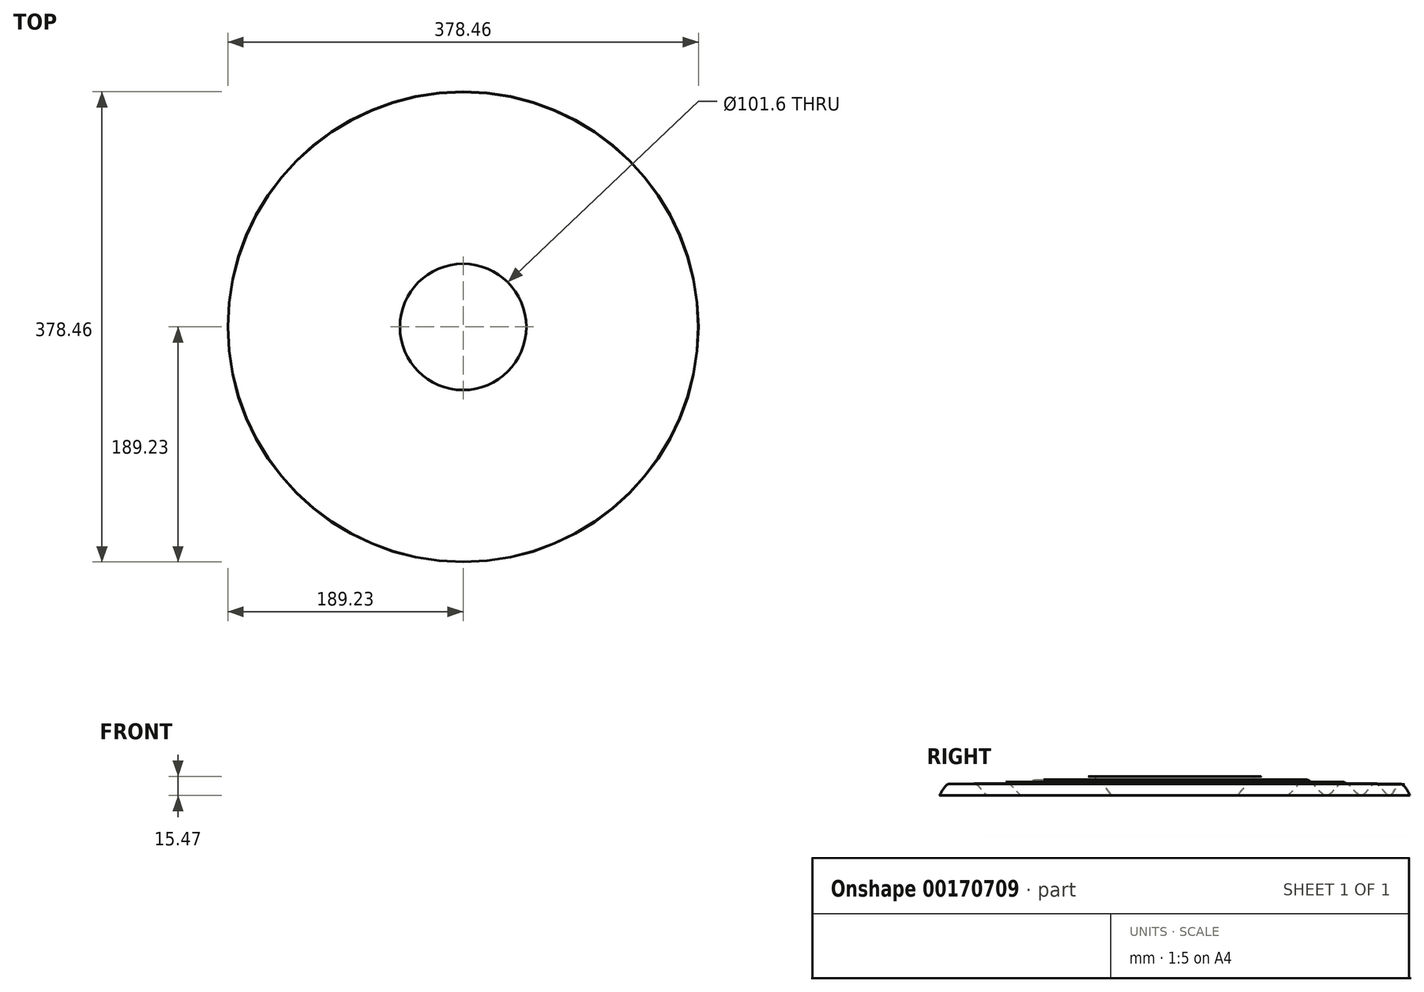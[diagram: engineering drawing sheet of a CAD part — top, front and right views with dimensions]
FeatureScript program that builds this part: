
annotation { "Feature Type Name" : "Feature", "Feature Type Description" : "" }
export const myFeature = defineFeature(function(context is Context, id is Id, definition is map)
    precondition{}
    {
        {
            var Q0;
            Q0=qCreatedBy(makeId("Front.planeOp"),FACE);
            var sketch = newSketch(context, id + "F0", { "sketchPlane" : qUnion([Q0])});
            skLineSegment(sketch, "E0", {"start": v(0, 51.98) * mm, "end": v(0, -57.5) * mm, "construction": true});
            skLineSegment(sketch, "E1", {"start": v(0, 38.1) * mm, "end": v(168.3, 13.53) * mm, "construction": true});
            skFitSpline(sketch, "E2", {"points": [v(50.8, 13.97) * mm, v(69.85, 27.9) * mm, v(88.9, 11.43) * mm, v(105.41, 22.71) * mm, v(121.92, 8.9) * mm, v(135.9, 18.26) * mm, v(149.86, 6.35) * mm, v(161.3, 14.55) * mm, v(172.72, 3.81) * mm, v(181.6, 11.59) * mm, v(189.23, 1.27) * mm], "startDerivative": vector(17.08, 50.9) * mm, "endDerivative": vector(25, -25.35) * mm, "construction": true});
            skFitSpline(sketch, "E3", {"points": [v(50.8, 0) * mm, v(69.85, 15.2) * mm, v(88.9, 0) * mm, v(105.41, 12.55) * mm, v(121.92, 0) * mm, v(135.9, 10.64) * mm, v(149.86, 0) * mm, v(161.3, 9.47) * mm, v(172.72, 0) * mm, v(181.61, 9.05) * mm, v(189.23, 0) * mm], "startDerivative": vector(16.8, 29.97) * mm, "endDerivative": vector(26.01, -29.79) * mm});
            skFitSpline(sketch, "E4", {"points": [v(50.8, 13.72) * mm, v(69.85, 27.65) * mm, v(88.9, 11.18) * mm, v(105.41, 22.46) * mm, v(121.92, 8.64) * mm, v(135.9, 18) * mm, v(149.86, 6.1) * mm, v(161.3, 14.3) * mm, v(172.72, 3.56) * mm, v(181.61, 11.33) * mm, v(189.23, 1.02) * mm], "startDerivative": vector(17.08, 35.58) * mm, "endDerivative": vector(22.25, -23.7) * mm, "construction": true});
            skLineSegment(sketch, "E5", {"start": v(50.8, 13.97) * mm, "end": v(50.8, 13.72) * mm, "construction": true});
            skLineSegment(sketch, "E6", {"start": v(189.23, 1.27) * mm, "end": v(189.23, 1.02) * mm, "construction": true});
            skFitSpline(sketch, "E7", {"points": [v(50.8, 0.25) * mm, v(69.85, 15.46) * mm, v(88.9, 0.25) * mm, v(105.41, 12.8) * mm, v(121.92, 0.25) * mm, v(135.9, 10.9) * mm, v(149.86, 0.25) * mm, v(161.29, 9.73) * mm, v(172.72, 0.25) * mm, v(181.61, 9.3) * mm, v(189.08, 0.25) * mm], "startDerivative": vector(18.41, 35.46) * mm, "endDerivative": vector(20.52, -36.15) * mm});
            skLineSegment(sketch, "E8", {"start": v(0, 0) * mm, "end": v(168.3, 0) * mm, "construction": true});
            skLineSegment(sketch, "E9", {"start": v(189.08, 0.25) * mm, "end": v(189.23, 0) * mm});
            skLineSegment(sketch, "E10", {"start": v(50.8, 0.25) * mm, "end": v(50.8, 0) * mm});
            skSolve(sketch);
        }
        {
            var Q0;
            Q0=makeQuery(id+"F0.imprint","IMPRINT",FACE,{"disambiguationData":[TD([[makeQuery(id+"F0.imprint","IMPRINT",EDGE,{"derivedFrom":sQuery(id+"F0.wireOp",EDGE,"E3")}),1.0]])]});
            var Q1;
            Q1=sQuery(id+"F0.wireOp",EDGE,"E0");
            revolve(context, id + "F1", {"entities" : qUnion([Q0]), "axis" : qUnion([Q1]), "revolveType" : RevolveType.FULL});
        }
    });
